# Revit family: DR1025551_SUBCJ_GF_LVM_MonocDraaMedia_Corona
name_source: partatom
category: Aparatos sanitarios
units: mm (PartAtom-declared; Revit-internal decimal feet)

## family parameters
Compartido = No
Corte con vacíos al cargar = No
Cota de conector redondo = Diámetro de uso
Número OmniClass = 23.31.11
Punto de cálculo de habitación = No
Se basa en plano de trabajo = No
Siempre vertical = Sí
Tipo de pieza = Normal

## types (1)
- DR1025551_SUBCJ_GF_LVM_MonocDraaMedia_Corona
    Acabado = Corona_Cromado
    Alto = 162 mm  [stored 0.531496 ft]
    Ancho = 160 mm
    Capacidad de flujo = 5,8 L/min.
    Caudal = 8,30 L/min
    Creado por = IDD
    Descripción = La línea Draa cuenta con todos los atributos de diseño y funcionalidad
que la hacen perfecta para soluciones en espacios actuales. Ofrece
una línea de griferías para ducha, lavamanos y accesorios con la
perfecta combinacion de líneas rectas y modernas.
    Diámetro = 35 mm  [stored 0.114829 ft]
    Fabricante = Corona
    Fecha de creación = 11/08/2020
    Garantía = 30 Años
    Garantía Acabados = 5 Años
    Peso neto = 1,20 kg. - 2,64 lb.
    Presion maxima = 125 psi (862 Kpa).
    Presion minima = 20 psi (138 Kpa).
    Referencia = DR1025551
    Temperatura de uso = 5ºC a 71ºC.
    URL = https://corona.co
    Vida útil = 500.000 ciclos.

note: [stored X ft] marks values corroborated as IEEE doubles in the binary element streams (Revit-internal decimal feet)

## geometry (parser evidence)
native form markers: Sweep x7
no freeform markers — native parametric forms only
